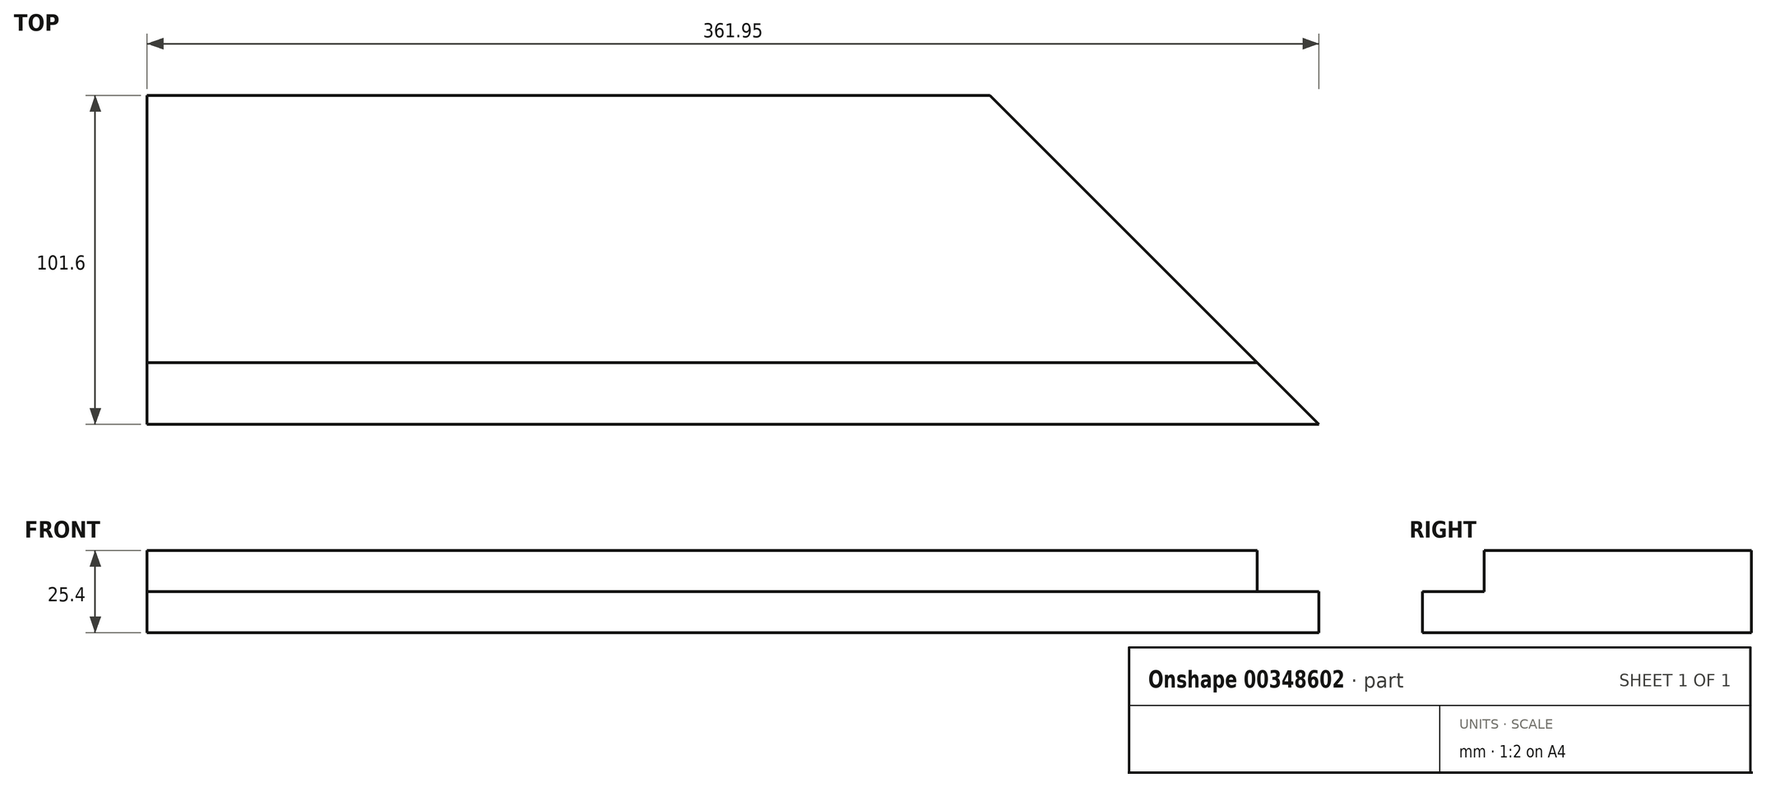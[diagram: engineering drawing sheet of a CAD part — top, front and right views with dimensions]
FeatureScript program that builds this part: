
annotation { "Feature Type Name" : "Feature", "Feature Type Description" : "" }
export const myFeature = defineFeature(function(context is Context, id is Id, definition is map)
    precondition{}
    {
        {
            var Q0;
            Q0=qCreatedBy(makeId("Top.planeOp"),FACE);
            var sketch = newSketch(context, id + "F0", { "sketchPlane" : qUnion([Q0])});
            skLineSegment(sketch, "E0", {"start": v(-119.49, 44.57) * mm, "end": v(140.86, 44.57) * mm});
            skLineSegment(sketch, "E1", {"start": v(-119.49, 44.57) * mm, "end": v(-119.49, -57.03) * mm});
            skLineSegment(sketch, "E2", {"start": v(-119.49, -57.03) * mm, "end": v(242.46, -57.03) * mm});
            skLineSegment(sketch, "E3", {"start": v(242.46, -57.03) * mm, "end": v(140.86, 44.57) * mm});
            skLineSegment(sketch, "E4", {"start": v(-119.49, -37.98) * mm, "end": v(223.41, -37.98) * mm});
            skSolve(sketch);
        }
        {
            var Q0;
            {var subQ0=sQuery(id+"F0.wireOp",EDGE,"E0");Q0=makeQuery(id+"F0.imprint","IMPRINT",FACE,{"disambiguationData":[TD([[makeQuery(id+"F0.imprint","IMPRINT",EDGE,{"derivedFrom":subQ0}),-1.0]])]});}
            extrude(context, id + "F1", {"entities" : qUnion([Q0]), "depth" : 12.7 * mm});
        }
        {
            var Q0;
            Q0 = qSketchRegion(id + "F0", true);
            var Q1;
            Q1=makeQuery(id+"F1.opExtrude","CAP_FACE",FACE,{"disambiguationData":[OSD([sQuery(id+"F0.wireOp",EDGE,"E0"),sQuery(id+"F0.wireOp",EDGE,"E1"),sQuery(id+"F0.wireOp",EDGE,"E3"),sQuery(id+"F0.wireOp",EDGE,"E4")])],"isStart":false});
            extrude(context, id + "F2", {"entities" : qUnion([Q0, Q1]), "operationType" : NewBodyOperationType.ADD, "depth" : 12.7 * mm});
        }
    });
